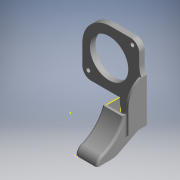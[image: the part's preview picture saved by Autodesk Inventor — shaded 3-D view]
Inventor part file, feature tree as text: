
AUTODESK INVENTOR PART (.ipt)
format: ipt  version: 2016 (Build 200138000, 138)  size: 1,155,072 bytes
history: native  units: mm (DEFAULTED — no unit token found)
features: sketch x6, fillet x5, other x3, projected_geometry x3, extrude x2, plane x2, hole x1
ambient origin geometry x8: Origin, YZ Plane, XZ Plane, XY Plane, X Axis, Y Axis, Z Axis, Center Point
bodies: Solid1 (feature_tree)
feature tree (22):
  other  "new wind guide3.iam"
  other  "base.ipt:1"
  other  "guide.ipt:1"
  extrude  "Extrusion1"  Depth=10.0mm
  fillet  "Fillet1"  Radius=2.0mm
  fillet  "Fillet2"  Radius=2.0mm
  fillet  "Fillet4"  Radius=1.59mm
  fillet  "Fillet5"  Radius=20.0mm
  extrude  "Extrusion2"  Depth=2.0mm TaperAngle=0.0deg
  hole  "Hole1"  [1 undecoded]
  fillet  "Fillet6"  [1 undecoded]
  plane  "Work Plane1"
  sketch  "Sketch2"  dims[d0=10.0mm d1=40.0mm d2=2.0mm d3=0.0mm d4=2.0mm d5=1.59mm d7=20.0mm]
  sketch  "Sketch4"  dims[d8=20.0mm d9=2.0mm d10=0.0mm]
  sketch  "Sketch5"  dims[d11=6.0mm d12=6.0mm d13=4.0mm d14=2.0mm d15=90.0deg d16=2.0mm d17=20.594885mm d18=50.0mm]
  plane  "Work Plane1_1"
  sketch  "Sketch6"
  projected_geometry  "Projected Loop1"
  sketch  "Sketch7"
  projected_geometry  "Projected Loop2"
  sketch  "Sketch8"
  projected_geometry  "Projected Loop3"
note: 2 required parameter values undecoded (feature->parameter linkage not recoverable at this tier; creation-order binding heuristic only, values carry confidence <= 0.55)
